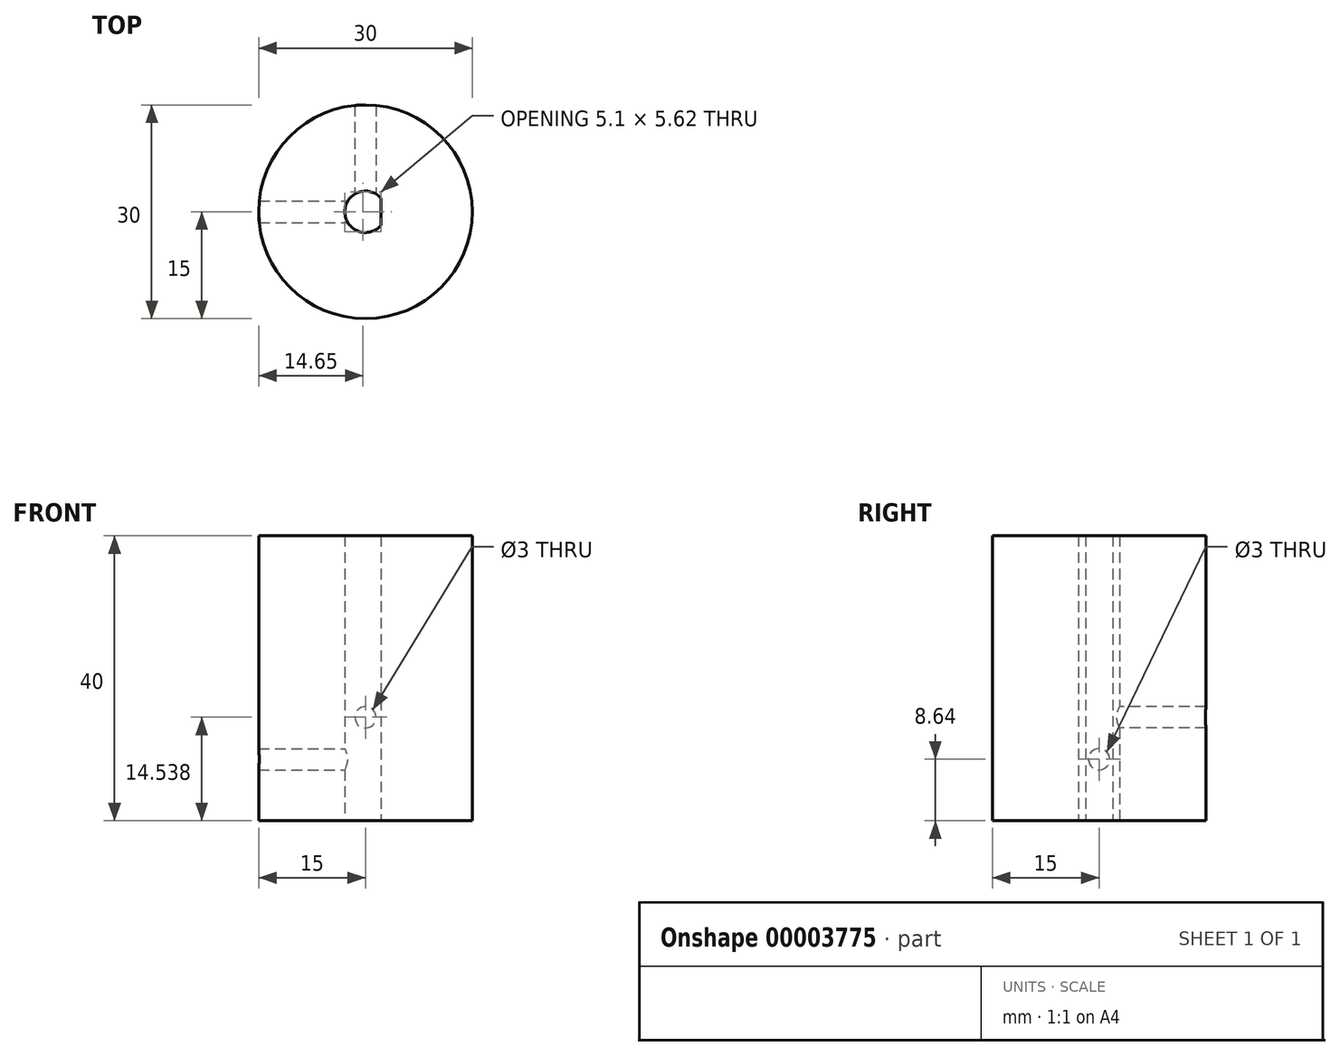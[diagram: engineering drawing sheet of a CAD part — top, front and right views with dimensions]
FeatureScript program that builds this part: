
annotation { "Feature Type Name" : "Feature", "Feature Type Description" : "" }
export const myFeature = defineFeature(function(context is Context, id is Id, definition is map)
    precondition{}
    {
        {
            var Q0;
            Q0=qCreatedBy(makeId("Top.planeOp"),FACE);
            var sketch = newSketch(context, id + "F0", { "sketchPlane" : qUnion([Q0])});
            skCircle(sketch, "E0", {"center": v(0, 0) * mm, "radius": 2.9 * mm});
            skCircle(sketch, "E1", {"center": v(0, 0) * mm, "radius": 15 * mm});
            skLineSegment(sketch, "E2", {"start": v(0, 15) * mm, "end": v(0, -15) * mm, "construction": true});
            skLineSegment(sketch, "E3", {"start": v(2.2, 1.89) * mm, "end": v(2.2, -1.89) * mm});
            skSolve(sketch);
        }
        {
            var Q0;
            Q0=makeQuery(id+"F0.imprint","IMPRINT",FACE,{"disambiguationData":[TD([[makeQuery(id+"F0.imprint","IMPRINT",EDGE,{"derivedFrom":sQuery(id+"F0.wireOp",EDGE,"E1")}),1.0]])]});
            var Q1;
            {var subQ0=sQuery(id+"F0.wireOp",EDGE,"E3");Q1=makeQuery(id+"F0.imprint","IMPRINT",FACE,{"disambiguationData":[TD([[makeQuery(id+"F0.imprint","IMPRINT",EDGE,{"derivedFrom":subQ0}),1.0]])]});}
            extrude(context, id + "F1", {"entities" : qUnion([Q0, Q1]), "depth" : 40 * mm});
        }
        {
            var Q0;
            Q0=qCreatedBy(makeId("Right.planeOp"),FACE);
            var sketch = newSketch(context, id + "F2", { "sketchPlane" : qUnion([Q0])});
            skLineSegment(sketch, "E4", {"start": v(0, 51.17) * mm, "end": v(0, 0) * mm, "construction": true});
            skCircle(sketch, "E5", {"center": v(0, 8.64) * mm, "radius": 1.5 * mm});
            skSolve(sketch);
        }
        {
            var Q0;
            Q0=qCreatedBy(makeId("Front.planeOp"),FACE);
            var sketch = newSketch(context, id + "F3", { "sketchPlane" : qUnion([Q0])});
            skCircle(sketch, "E6", {"center": v(0, 14.54) * mm, "radius": 1.5 * mm});
            skSolve(sketch);
        }
        {
            var Q0;
            Q0 = qSketchRegion(id + "F3", true);
            extrude(context, id + "F4", {"entities" : qUnion([Q0]), "operationType" : NewBodyOperationType.REMOVE, "oppositeDirection" : true, "depth" : 25 * mm});
        }
        {
            var Q0;
            Q0 = qSketchRegion(id + "F2", true);
            extrude(context, id + "F5", {"entities" : qUnion([Q0]), "operationType" : NewBodyOperationType.REMOVE, "oppositeDirection" : true, "depth" : 25 * mm});
        }
    });
